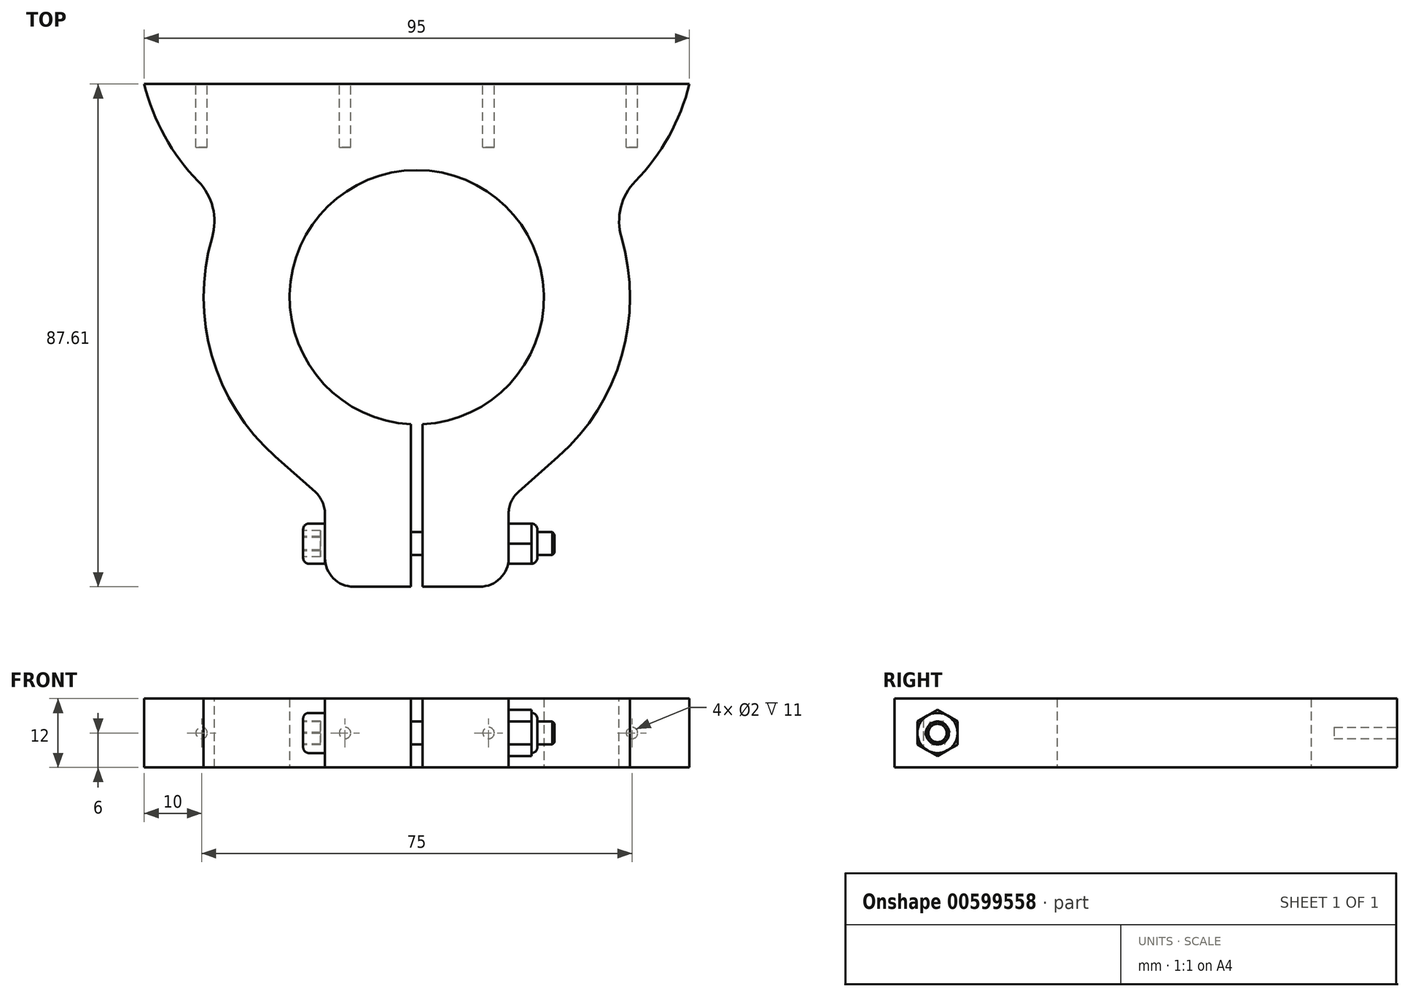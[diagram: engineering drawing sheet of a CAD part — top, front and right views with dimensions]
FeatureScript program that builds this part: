
annotation { "Feature Type Name" : "Feature", "Feature Type Description" : "" }
export const myFeature = defineFeature(function(context is Context, id is Id, definition is map)
    precondition{}
    {
        {
            var Q0;
            Q0=qCreatedBy(makeId("Top.planeOp"),FACE);
            var sketch = newSketch(context, id + "F0", { "sketchPlane" : qUnion([Q0])});
            skLineSegment(sketch, "E0", {"start": v(-47.5, 0) * mm, "end": v(47.5, 0) * mm});
            skLineSegment(sketch, "E1", {"start": v(-47.5, 0) * mm, "end": v(-33.28, -57.3) * mm});
            skLineSegment(sketch, "E2", {"start": v(-33.28, -57.3) * mm, "end": v(-16, -72.6) * mm});
            skLineSegment(sketch, "E3", {"start": v(-16, -72.6) * mm, "end": v(-16, -87.6) * mm});
            skLineSegment(sketch, "E4", {"start": v(-16, -87.6) * mm, "end": v(-1, -87.6) * mm});
            skLineSegment(sketch, "E5", {"start": v(-1, -87.6) * mm, "end": v(-1, -59.28) * mm});
            skArc(sketch, "E6", {"start": v(1, -59.28) * mm, "mid": v(0, -15) * mm, "end": v(-1, -59.28) * mm});
            skLineSegment(sketch, "E7.MirrorCS", {"start": v(47.5, 0) * mm, "end": v(33.28, -57.3) * mm});
            skLineSegment(sketch, "E8.MirrorCS", {"start": v(33.28, -57.3) * mm, "end": v(16, -72.6) * mm});
            skLineSegment(sketch, "E9.MirrorCS", {"start": v(16, -72.6) * mm, "end": v(16, -87.6) * mm});
            skLineSegment(sketch, "E10.MirrorCS", {"start": v(16, -87.6) * mm, "end": v(1, -87.6) * mm});
            skLineSegment(sketch, "E11.MirrorCS", {"start": v(1, -87.6) * mm, "end": v(1, -59.28) * mm});
            skCircle(sketch, "E12", {"center": v(0, -37.15) * mm, "radius": 37.15 * mm, "construction": true});
            skLineSegment(sketch, "E13", {"start": v(0, -37.15) * mm, "end": v(-24.64, -64.95) * mm, "construction": true});
            skSolve(sketch);
        }
        {
            var Q0;
            Q0 = qSketchRegion(id + "F0", true);
            extrude(context, id + "F1", {"entities" : qUnion([Q0]), "depth" : 12 * mm, "offsetDistance" : 25 * mm});
        }
        {
            var Q0;
            Q0=makeQuery(id+"F1.opExtrude","SWEPT_EDGE",EDGE,{"disambiguationData":[OSD([sQuery(id+"F0.wireOp",EDGE,"E1"),sQuery(id+"F0.wireOp",EDGE,"E2")])]});
            var Q1;
            Q1=makeQuery(id+"F1.opExtrude","SWEPT_EDGE",EDGE,{"disambiguationData":[OSD([sQuery(id+"F0.wireOp",EDGE,"E7.MirrorCS"),sQuery(id+"F0.wireOp",EDGE,"E8.MirrorCS")])]});
            fillet(context, id + "F2", {"entities" : qUnion([Q0, Q1]), "radius" : (74.3 / 2) * mm, "tangentPropagation" : true, "allowEdgeOverflow" : false});
        }
        {
            var Q0;
            Q0=makeQuery(id+"F1.opExtrude","SWEPT_FACE",FACE,{"disambiguationData":[OSD([sQuery(id+"F0.wireOp",EDGE,"E3")])]});
            var sketch = newSketch(context, id + "F3", { "sketchPlane" : qUnion([Q0])});
            skCircle(sketch, "E14", {"center": v(80.1, 6) * mm, "radius": 2 * mm});
            skPoint(sketch, "E14.centerSnap0", {"position": v(87.6, 6) * mm});
            skSolve(sketch);
        }
        {
            var Q0;
            Q0 = qSketchRegion(id + "F3", true);
            extrude(context, id + "F4", {"entities" : qUnion([Q0]), "operationType" : NewBodyOperationType.REMOVE, "endBound" : BoundingType.THROUGH_ALL, "oppositeDirection" : true, "depth" : 25 * mm, "offsetDistance" : 25 * mm});
        }
        {
            var Q0;
            Q0=makeQuery(id+"F1.opExtrude","SWEPT_EDGE",EDGE,{"disambiguationData":[OSD([sQuery(id+"F0.wireOp",EDGE,"E2"),sQuery(id+"F0.wireOp",EDGE,"E3")])]});
            var Q1;
            Q1=makeQuery(id+"F1.opExtrude","SWEPT_EDGE",EDGE,{"disambiguationData":[OSD([sQuery(id+"F0.wireOp",EDGE,"E3"),sQuery(id+"F0.wireOp",EDGE,"E4")])]});
            var Q2;
            Q2=makeQuery(id+"F1.opExtrude","SWEPT_EDGE",EDGE,{"disambiguationData":[OSD([sQuery(id+"F0.wireOp",EDGE,"E9.MirrorCS"),sQuery(id+"F0.wireOp",EDGE,"E10.MirrorCS")])]});
            var Q3;
            Q3=makeQuery(id+"F1.opExtrude","SWEPT_EDGE",EDGE,{"disambiguationData":[OSD([sQuery(id+"F0.wireOp",EDGE,"E8.MirrorCS"),sQuery(id+"F0.wireOp",EDGE,"E9.MirrorCS")])]});
            fillet(context, id + "F5", {"entities" : qUnion([Q0, Q1, Q2, Q3]), "radius" : 5 * mm, "tangentPropagation" : true, "allowEdgeOverflow" : false});
        }
        {
            var Q0;
            Q0=makeQuery(id+"F1.opExtrude","SWEPT_FACE",FACE,{"disambiguationData":[OSD([sQuery(id+"F0.wireOp",EDGE,"E3")])]});
            var sketch = newSketch(context, id + "F6", { "sketchPlane" : qUnion([Q0])});
            skCircle(sketch, "E15", {"center": v(80.1, 6) * mm, "radius": 3.5 * mm});
            skSolve(sketch);
        }
        {
            var Q0;
            Q0 = qSketchRegion(id + "F6", true);
            extrude(context, id + "F7", {"entities" : qUnion([Q0]), "depth" : 3.8 * mm, "offsetDistance" : 25 * mm});
        }
        {
            var Q0;
            Q0=makeQuery(id+"F7.opExtrude","CAP_FACE",FACE,{"disambiguationData":[OSD([sQuery(id+"F6.wireOp",EDGE,"E15")])],"isStart":true});
            var sketch = newSketch(context, id + "F8", { "sketchPlane" : qUnion([Q0])});
            skCircle(sketch, "E16", {"center": v(-80.1, 6) * mm, "radius": 2 * mm});
            skSolve(sketch);
        }
        {
            var Q0;
            Q0 = qSketchRegion(id + "F8", true);
            extrude(context, id + "F9", {"entities" : qUnion([Q0]), "operationType" : NewBodyOperationType.ADD, "depth" : 40 * mm, "offsetDistance" : 25 * mm});
        }
        {
            var Q0;
            Q0=makeQuery(id+"F1.opExtrude","SWEPT_FACE",FACE,{"disambiguationData":[OSD([sQuery(id+"F0.wireOp",EDGE,"E9.MirrorCS")])]});
            var sketch = newSketch(context, id + "F10", { "sketchPlane" : qUnion([Q0])});
            skCircle(sketch, "E17.cCircle", {"center": v(-80.1, 6) * mm, "radius": 3.5 * mm, "construction": true});
            skLineSegment(sketch, "E17.0", {"start": v(-80.12, 1.96) * mm, "end": v(-83.62, 4) * mm});
            skLineSegment(sketch, "E17.1", {"start": v(-83.62, 4) * mm, "end": v(-83.6, 8.03) * mm});
            skLineSegment(sketch, "E17.2", {"start": v(-83.6, 8.03) * mm, "end": v(-80.1, 10.04) * mm});
            skLineSegment(sketch, "E17.3", {"start": v(-80.1, 10.04) * mm, "end": v(-76.6, 8) * mm});
            skLineSegment(sketch, "E17.4", {"start": v(-76.6, 8) * mm, "end": v(-76.62, 3.97) * mm});
            skLineSegment(sketch, "E17.5", {"start": v(-76.62, 3.97) * mm, "end": v(-80.12, 1.96) * mm});
            skPoint(sketch, "E17.0.midPoint", {"position": v(-81.87, 2.97) * mm});
            skCircle(sketch, "E18", {"center": v(-80.1, 6) * mm, "radius": 2 * mm});
            skSolve(sketch);
        }
        {
            var Q0;
            Q0 = qSketchRegion(id + "F10", true);
            extrude(context, id + "F11", {"entities" : qUnion([Q0]), "depth" : 4 * mm, "offsetDistance" : 25 * mm});
        }
        {
            var Q0;
            Q0=makeQuery(id+"F11.opExtrude","CAP_FACE",FACE,{"disambiguationData":[OSD([sQuery(id+"F10.wireOp",EDGE,"E17.0"),sQuery(id+"F10.wireOp",EDGE,"E17.1"),sQuery(id+"F10.wireOp",EDGE,"E17.2"),sQuery(id+"F10.wireOp",EDGE,"E17.3"),sQuery(id+"F10.wireOp",EDGE,"E17.4"),sQuery(id+"F10.wireOp",EDGE,"E17.5"),sQuery(id+"F10.wireOp",EDGE,"E18")])],"isStart":false});
            var sketch = newSketch(context, id + "F12", { "sketchPlane" : qUnion([Q0])});
            skCircle(sketch, "E19", {"center": v(-80.1, 6) * mm, "radius": 3.5 * mm});
            skCircle(sketch, "E20", {"center": v(-80.1, 6) * mm, "radius": 2 * mm});
            skSolve(sketch);
        }
        {
            var Q0;
            Q0 = qSketchRegion(id + "F12", true);
            extrude(context, id + "F13", {"entities" : qUnion([Q0]), "operationType" : NewBodyOperationType.ADD, "depth" : 1 * mm, "offsetDistance" : 25 * mm});
        }
        {
            var Q0;
            {var subQ0=sQuery(id+"F12.wireOp",EDGE,"E19");var subQ1=makeQuery(id+"F11.opExtrude","CAP_EDGE",EDGE,{"disambiguationData":[OSD([sQuery(id+"F10.wireOp",EDGE,"E17.4")])],"isStart":false});var subQ2=makeQuery(id+"F12.imprint","INTERSECT",VERTEX,{"derivedFrom":[makeQuery(id+"F11.opExtrude","CAP_EDGE",EDGE,{"disambiguationData":[OSD([sQuery(id+"F10.wireOp",EDGE,"E17.5")])],"isStart":false}),subQ0]});var subQ3=makeQuery(id+"F12.imprint","INTERSECT",VERTEX,{"derivedFrom":[makeQuery(id+"F11.opExtrude","CAP_EDGE",EDGE,{"disambiguationData":[OSD([sQuery(id+"F10.wireOp",EDGE,"E17.0")])],"isStart":false}),subQ0]});var subQ4=makeQuery(id+"F12.imprint","INTERSECT",VERTEX,{"derivedFrom":[makeQuery(id+"F11.opExtrude","CAP_EDGE",EDGE,{"disambiguationData":[OSD([sQuery(id+"F10.wireOp",EDGE,"E17.1")])],"isStart":false}),subQ0]});var subQ5=makeQuery(id+"F12.imprint","INTERSECT",VERTEX,{"derivedFrom":[makeQuery(id+"F11.opExtrude","CAP_EDGE",EDGE,{"disambiguationData":[OSD([sQuery(id+"F10.wireOp",EDGE,"E17.2")])],"isStart":false}),subQ0]});var subQ6=makeQuery(id+"F12.imprint","INTERSECT",VERTEX,{"derivedFrom":[makeQuery(id+"F11.opExtrude","CAP_EDGE",EDGE,{"disambiguationData":[OSD([sQuery(id+"F10.wireOp",EDGE,"E17.3")])],"isStart":false}),subQ0]});Q0=makeQuery(id+"F13.opExtrude","CAP_EDGE",EDGE,{"disambiguationData":[OSD([subQ0]),TDD([makeQuery(id+"F12.imprint","IMPRINT",EDGE,{"disambiguationData":[TD([[makeQuery(id+"F12.imprint","INTERSECT",VERTEX,{"disambiguationData":[OD(0.0)],"derivedFrom":[subQ1,subQ0]}),-1.0],[subQ6,1.0]])],"derivedFrom":subQ0}),makeQuery(id+"F12.imprint","IMPRINT",EDGE,{"disambiguationData":[TD([[subQ6,-1.0],[subQ5,1.0]])],"derivedFrom":subQ0}),makeQuery(id+"F12.imprint","IMPRINT",EDGE,{"disambiguationData":[TD([[subQ5,-1.0],[subQ4,1.0]])],"derivedFrom":subQ0}),makeQuery(id+"F12.imprint","IMPRINT",EDGE,{"disambiguationData":[TD([[subQ4,-1.0],[subQ3,1.0]])],"derivedFrom":subQ0}),makeQuery(id+"F12.imprint","IMPRINT",EDGE,{"disambiguationData":[TD([[subQ3,-1.0],[subQ2,1.0]])],"derivedFrom":subQ0}),makeQuery(id+"F12.imprint","IMPRINT",EDGE,{"disambiguationData":[TD([[makeQuery(id+"F12.imprint","INTERSECT",VERTEX,{"disambiguationData":[OD(1.0)],"derivedFrom":[subQ1,subQ0]}),1.0],[subQ2,-1.0]])],"derivedFrom":subQ0})])],"isStart":false});}
            fillet(context, id + "F14", {"entities" : qUnion([Q0]), "radius" : 1 * mm, "tangentPropagation" : true, "allowEdgeOverflow" : false});
        }
        {
            var Q0;
            Q0=makeQuery(id+"F9.opExtrude","CAP_EDGE",EDGE,{"disambiguationData":[OSD([sQuery(id+"F8.wireOp",EDGE,"E16")])],"isStart":false});
            chamfer(context, id + "F15", {"entities" : qUnion([Q0]), "width" : 0.4 * mm, "tangentPropagation" : true});
        }
        {
            var Q0;
            Q0=makeQuery(id+"F7.opExtrude","CAP_FACE",FACE,{"disambiguationData":[OSD([sQuery(id+"F6.wireOp",EDGE,"E15")])],"isStart":false});
            var sketch = newSketch(context, id + "F16", { "sketchPlane" : qUnion([Q0])});
            skCircle(sketch, "E21.cCircle", {"center": v(80.1, 6) * mm, "radius": 2 * mm, "construction": true});
            skLineSegment(sketch, "E21.0", {"start": v(82.42, 5.9) * mm, "end": v(81.17, 3.95) * mm});
            skLineSegment(sketch, "E21.1", {"start": v(81.17, 3.95) * mm, "end": v(78.86, 4.06) * mm});
            skLineSegment(sketch, "E21.2", {"start": v(78.86, 4.06) * mm, "end": v(77.8, 6.1) * mm});
            skLineSegment(sketch, "E21.3", {"start": v(77.8, 6.1) * mm, "end": v(79.05, 8.05) * mm});
            skLineSegment(sketch, "E21.4", {"start": v(79.05, 8.05) * mm, "end": v(81.36, 7.94) * mm});
            skLineSegment(sketch, "E21.5", {"start": v(81.36, 7.94) * mm, "end": v(82.42, 5.9) * mm});
            skPoint(sketch, "E21.0.midPoint", {"position": v(81.8, 4.92) * mm});
            skSolve(sketch);
        }
        {
            var Q0;
            Q0 = qSketchRegion(id + "F16", true);
            extrude(context, id + "F17", {"entities" : qUnion([Q0]), "operationType" : NewBodyOperationType.REMOVE, "oppositeDirection" : true, "depth" : 3 * mm, "offsetDistance" : 25 * mm});
        }
        {
            var Q0;
            Q0=makeQuery(id+"F7.opExtrude","CAP_EDGE",EDGE,{"disambiguationData":[OSD([sQuery(id+"F6.wireOp",EDGE,"E15")])],"isStart":false});
            fillet(context, id + "F18", {"entities" : qUnion([Q0]), "radius" : 1 * mm, "tangentPropagation" : true, "allowEdgeOverflow" : false});
        }
        {
            var Q0;
            Q0=makeQuery(id+"F1.opExtrude","CAP_FACE",FACE,{"disambiguationData":[OSD([sQuery(id+"F0.wireOp",EDGE,"E0"),sQuery(id+"F0.wireOp",EDGE,"E1"),sQuery(id+"F0.wireOp",EDGE,"E2"),sQuery(id+"F0.wireOp",EDGE,"E3"),sQuery(id+"F0.wireOp",EDGE,"E4"),sQuery(id+"F0.wireOp",EDGE,"E5"),sQuery(id+"F0.wireOp",EDGE,"E6"),sQuery(id+"F0.wireOp",EDGE,"E7.MirrorCS"),sQuery(id+"F0.wireOp",EDGE,"E8.MirrorCS"),sQuery(id+"F0.wireOp",EDGE,"E9.MirrorCS"),sQuery(id+"F0.wireOp",EDGE,"E10.MirrorCS"),sQuery(id+"F0.wireOp",EDGE,"E11.MirrorCS")])],"isStart":false});
            var sketch = newSketch(context, id + "F19", { "sketchPlane" : qUnion([Q0])});
            skLineSegment(sketch, "E22", {"start": v(-47.5, 0) * mm, "end": v(-36.06, -46.1) * mm});
            skPoint(sketch, "E23.visualSharp", {"position": v(-38.68, -27.58) * mm});
            skLineSegment(sketch, "E24", {"start": v(0, 0) * mm, "end": v(0, -37.15) * mm, "construction": true});
            skArc(sketch, "E25", {"start": v(-35.66, -26.72) * mm, "mid": v(-37.14, -36.38) * mm, "end": v(-36.06, -46.1) * mm});
            skArc(sketch, "E26", {"start": v(-47.5, 0) * mm, "mid": v(-43.92, -9.1) * mm, "end": v(-38.08, -16.94) * mm});
            skLineSegment(sketch, "E27", {"start": v(-11.44, 8.95) * mm, "end": v(-47.5, 0) * mm, "construction": true});
            skPoint(sketch, "E28.visualSharp", {"position": v(-33.45, -20.98) * mm});
            skArc(sketch, "E28.filletArc", {"start": v(-35.66, -26.72) * mm, "mid": v(-35.55, -21.5) * mm, "end": v(-38.08, -16.94) * mm});
            skArc(sketch, "E29.MirrorCS", {"start": v(35.66, -26.72) * mm, "mid": v(37.14, -36.38) * mm, "end": v(36.06, -46.1) * mm});
            skArc(sketch, "E30.MirrorCS", {"start": v(35.66, -26.72) * mm, "mid": v(35.55, -21.5) * mm, "end": v(38.08, -16.94) * mm});
            skArc(sketch, "E31.MirrorCS", {"start": v(47.5, 0) * mm, "mid": v(43.92, -9.1) * mm, "end": v(38.08, -16.94) * mm});
            skLineSegment(sketch, "E32.MirrorCS", {"start": v(47.5, 0) * mm, "end": v(36.06, -46.1) * mm});
            skSolve(sketch);
        }
        {
            var Q0;
            Q0 = qSketchRegion(id + "F19", true);
            extrude(context, id + "F20", {"entities" : qUnion([Q0]), "operationType" : NewBodyOperationType.REMOVE, "endBound" : BoundingType.THROUGH_ALL, "oppositeDirection" : true, "depth" : 25 * mm, "offsetDistance" : 25 * mm});
        }
        {
            var Q0;
            Q0=makeQuery(id+"F1.opExtrude","SWEPT_FACE",FACE,{"disambiguationData":[OSD([sQuery(id+"F0.wireOp",EDGE,"E0")])]});
            var sketch = newSketch(context, id + "F21", { "sketchPlane" : qUnion([Q0])});
            skCircle(sketch, "E33", {"center": v(-37.5, 6) * mm, "radius": 1 * mm});
            skPoint(sketch, "E33.centerSnap0", {"position": v(-47.5, 6) * mm});
            skCircle(sketch, "E34.1.0.0", {"center": v(-12.5, 6) * mm, "radius": 1 * mm});
            skCircle(sketch, "E34.2.0.0", {"center": v(12.5, 6) * mm, "radius": 1 * mm});
            skCircle(sketch, "E34.3.0.0", {"center": v(37.5, 6) * mm, "radius": 1 * mm});
            skLineSegment(sketch, "E34.direction1", {"start": v(-37.5, 6) * mm, "end": v(-12.5, 6) * mm, "construction": true});
            skLineSegment(sketch, "E35", {"start": v(-37.5, 6) * mm, "end": v(-47.5, 6) * mm, "construction": true});
            skLineSegment(sketch, "E36", {"start": v(47.5, 6) * mm, "end": v(37.5, 6) * mm, "construction": true});
            skSolve(sketch);
        }
        {
            var Q0;
            Q0 = qSketchRegion(id + "F21", true);
            extrude(context, id + "F22", {"entities" : qUnion([Q0]), "operationType" : NewBodyOperationType.REMOVE, "oppositeDirection" : true, "depth" : 11 * mm, "offsetDistance" : 25 * mm});
        }
    });
